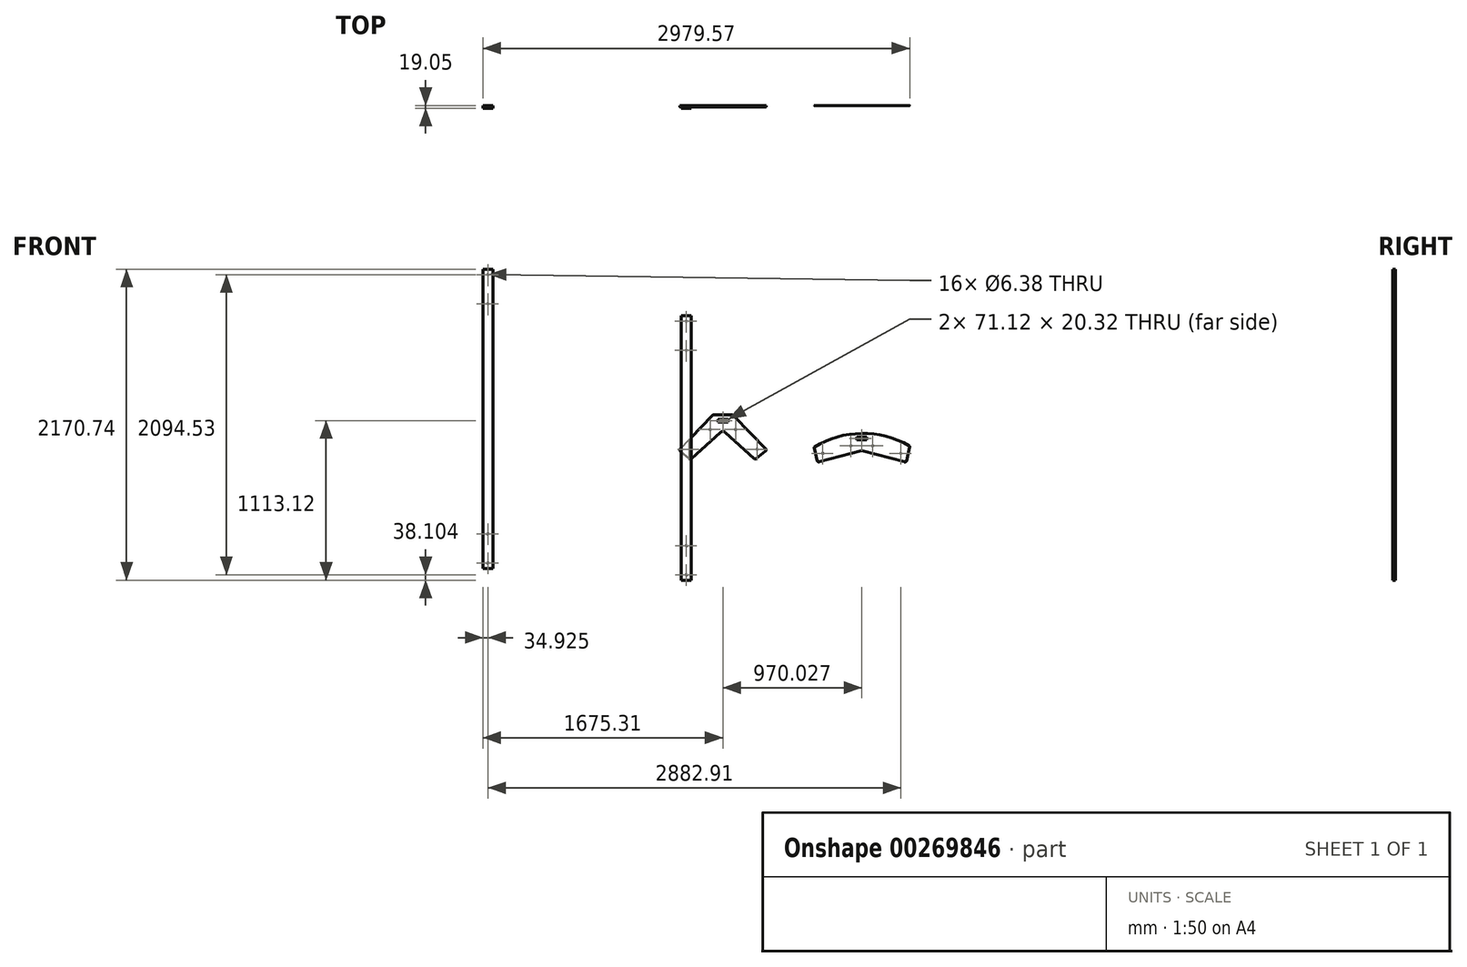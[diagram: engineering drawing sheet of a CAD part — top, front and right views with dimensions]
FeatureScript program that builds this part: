
annotation { "Feature Type Name" : "Feature", "Feature Type Description" : "" }
export const myFeature = defineFeature(function(context is Context, id is Id, definition is map)
    precondition{}
    {
        {
            var Q0;
            Q0=qCreatedBy(makeId("Front.planeOp"),FACE);
            var sketch = newSketch(context, id + "F0", { "sketchPlane" : qUnion([Q0])});
            skLineSegment(sketch, "E0.bottom", {"start": v(-21.12, -905.57) * mm, "end": v(-90.97, -905.57) * mm});
            skLineSegment(sketch, "E0.top", {"start": v(-21.12, 939.7) * mm, "end": v(-90.97, 939.7) * mm});
            skLineSegment(sketch, "E0.left", {"start": v(-21.12, -905.57) * mm, "end": v(-21.12, 939.7) * mm});
            skLineSegment(sketch, "E0.right", {"start": v(-90.97, -905.57) * mm, "end": v(-90.97, 939.7) * mm});
            skLineSegment(sketch, "E1.bottom", {"start": v(-1404.82, -823.6) * mm, "end": v(-1474.67, -823.6) * mm});
            skLineSegment(sketch, "E1.top", {"start": v(-1404.82, 1265.17) * mm, "end": v(-1474.67, 1265.17) * mm});
            skLineSegment(sketch, "E1.left", {"start": v(-1404.82, -823.6) * mm, "end": v(-1404.82, 1265.17) * mm});
            skLineSegment(sketch, "E1.right", {"start": v(-1474.67, -823.6) * mm, "end": v(-1474.67, 1265.17) * mm});
            skLineSegment(sketch, "E2", {"start": v(1170.66, 233.89) * mm, "end": v(1170.66, 0) * mm, "construction": true});
            skLineSegment(sketch, "E3", {"start": v(838.18, 14.85) * mm, "end": v(857.28, -70.28) * mm});
            skLineSegment(sketch, "E4", {"start": v(872.96, -79.77) * mm, "end": v(1167.38, -0.88) * mm});
            skLineSegment(sketch, "E5.MirrorCS", {"start": v(1504.59, 21.27) * mm, "end": v(1484.04, -70.28) * mm});
            skLineSegment(sketch, "E6.MirrorCS", {"start": v(1468.36, -79.77) * mm, "end": v(1173.95, -0.88) * mm});
            skLineSegment(sketch, "E7.bottom", {"start": v(1135.1, 73.36) * mm, "end": v(1206.22, 73.36) * mm});
            skLineSegment(sketch, "E7.top", {"start": v(1135.1, 93.68) * mm, "end": v(1206.22, 93.68) * mm});
            skLineSegment(sketch, "E7.left", {"start": v(1135.1, 73.36) * mm, "end": v(1135.1, 93.68) * mm});
            skLineSegment(sketch, "E7.right", {"start": v(1206.22, 73.36) * mm, "end": v(1206.22, 93.68) * mm});
            skPoint(sketch, "E7.middle", {"position": v(1170.66, 83.52) * mm});
            skPoint(sketch, "E8.visualSharp", {"position": v(1170.66, 0) * mm});
            skArc(sketch, "E8.filletArc", {"start": v(1173.95, -0.88) * mm, "mid": v(1170.66, -0.45) * mm, "end": v(1167.38, -0.88) * mm});
            skPoint(sketch, "E9.visualSharp", {"position": v(1481.15, -83.2) * mm});
            skArc(sketch, "E9.filletArc", {"start": v(1468.36, -79.77) * mm, "mid": v(1478.23, -78.37) * mm, "end": v(1484.04, -70.28) * mm});
            skPoint(sketch, "E10.visualSharp", {"position": v(860.18, -83.2) * mm});
            skArc(sketch, "E10.filletArc", {"start": v(857.28, -70.28) * mm, "mid": v(863.1, -78.37) * mm, "end": v(872.96, -79.77) * mm});
            skPoint(sketch, "E11.visualSharp", {"position": v(837.93, 15.94) * mm});
            skArc(sketch, "E11.filletArc", {"start": v(839.67, 24.15) * mm, "mid": v(838.03, 19.64) * mm, "end": v(838.18, 14.85) * mm});
            skPoint(sketch, "E12.visualSharp", {"position": v(1503.4, 15.94) * mm});
            skArc(sketch, "E12.filletArc", {"start": v(1504.59, 21.27) * mm, "mid": v(1504.22, 28.15) * mm, "end": v(1500.3, 33.82) * mm});
            skArc(sketch, "E13", {"start": v(1500.3, 33.82) * mm, "mid": v(1168.67, 119) * mm, "end": v(839.67, 24.15) * mm});
            skPoint(sketch, "E14", {"position": v(898.16, -20.43) * mm});
            skPoint(sketch, "E15", {"position": v(1094.44, 32.17) * mm});
            skCircle(sketch, "E16", {"center": v(898.16, -20.43) * mm, "radius": 3.19 * mm});
            skCircle(sketch, "E17", {"center": v(1094.44, 32.17) * mm, "radius": 3.19 * mm});
            skCircle(sketch, "E18.MirrorC", {"center": v(1246.9, 32.17) * mm, "radius": 3.19 * mm});
            skPoint(sketch, "E19.MirrorP", {"position": v(1443.17, -20.43) * mm});
            skCircle(sketch, "E20.MirrorC", {"center": v(1443.17, -20.43) * mm, "radius": 3.19 * mm});
            skCircle(sketch, "E21", {"center": v(-1439.74, 1227.07) * mm, "radius": 3.19 * mm});
            skCircle(sketch, "E22", {"center": v(-1439.74, 1023.87) * mm, "radius": 3.19 * mm});
            skCircle(sketch, "E23", {"center": v(-1439.74, -582.3) * mm, "radius": 3.19 * mm});
            skCircle(sketch, "E24", {"center": v(-1439.74, -785.5) * mm, "radius": 3.19 * mm});
            skCircle(sketch, "E25", {"center": v(-56.04, 901.6) * mm, "radius": 3.19 * mm});
            skCircle(sketch, "E26", {"center": v(-56.04, 698.4) * mm, "radius": 3.19 * mm});
            skCircle(sketch, "E27", {"center": v(-55.4, -664.27) * mm, "radius": 3.19 * mm});
            skCircle(sketch, "E28", {"center": v(-55.4, -867.47) * mm, "radius": 3.19 * mm});
            skSolve(sketch);
        }
        {
            var Q0;
            Q0=makeQuery(id+"F0.imprint","IMPRINT",FACE,{"disambiguationData":[TD([[makeQuery(id+"F0.imprint","IMPRINT",EDGE,{"derivedFrom":sQuery(id+"F0.wireOp",EDGE,"E3")}),1.0]])]});
            extrude(context, id + "F1", {"entities" : qUnion([Q0]), "depth" : 3 / 203.2 * mm});
        }
        {
            var Q0;
            Q0=qCreatedBy(makeId("Front.planeOp"),FACE);
            var sketch = newSketch(context, id + "F2", { "sketchPlane" : qUnion([Q0])});
            skLineSegment(sketch, "E29.bottom", {"start": v(-2314.97, -814.36) * mm, "end": v(-2384.82, -814.36) * mm});
            skLineSegment(sketch, "E29.top", {"start": v(-2314.97, 1274.41) * mm, "end": v(-2384.82, 1274.41) * mm});
            skLineSegment(sketch, "E29.left", {"start": v(-2314.97, -814.36) * mm, "end": v(-2314.97, 1274.41) * mm});
            skLineSegment(sketch, "E29.right", {"start": v(-2384.82, -814.36) * mm, "end": v(-2384.82, 1274.41) * mm});
            skLineSegment(sketch, "E30", {"start": v(200.64, 320.87) * mm, "end": v(200.64, 91.06) * mm, "construction": true});
            skLineSegment(sketch, "E31", {"start": v(-96.8, -4.89) * mm, "end": v(-32.6, -57.3) * mm});
            skLineSegment(sketch, "E32", {"start": v(-15.98, -56.83) * mm, "end": v(183.48, 125.94) * mm});
            skLineSegment(sketch, "E33.MirrorCS", {"start": v(417.26, -56.83) * mm, "end": v(217.8, 125.94) * mm});
            skLineSegment(sketch, "E34.MirrorCS", {"start": v(498.07, -4.89) * mm, "end": v(433.87, -57.3) * mm});
            skPoint(sketch, "E35.visualSharp", {"position": v(200.64, 141.66) * mm});
            skArc(sketch, "E35.filletArc", {"start": v(217.8, 125.94) * mm, "mid": v(200.64, 132.61) * mm, "end": v(183.48, 125.94) * mm});
            skPoint(sketch, "E36.visualSharp", {"position": v(-102.78, 0) * mm});
            skArc(sketch, "E36.filletArc", {"start": v(-101.16, 7.72) * mm, "mid": v(-100.77, 0.8) * mm, "end": v(-96.8, -4.89) * mm});
            skPoint(sketch, "E37.visualSharp", {"position": v(-24.09, -64.26) * mm});
            skArc(sketch, "E37.filletArc", {"start": v(-32.6, -57.3) * mm, "mid": v(-24.2, -60.17) * mm, "end": v(-15.98, -56.83) * mm});
            skPoint(sketch, "E38.visualSharp", {"position": v(425.36, -64.26) * mm});
            skArc(sketch, "E38.filletArc", {"start": v(417.26, -56.83) * mm, "mid": v(425.48, -60.17) * mm, "end": v(433.87, -57.3) * mm});
            skPoint(sketch, "E39.visualSharp", {"position": v(504.06, 0) * mm});
            skArc(sketch, "E39.filletArc", {"start": v(498.07, -4.89) * mm, "mid": v(502.04, 0.8) * mm, "end": v(502.43, 7.72) * mm});
            skPoint(sketch, "E40", {"position": v(-38.08, 9.05) * mm});
            skPoint(sketch, "E41", {"position": v(111.74, 146.33) * mm});
            skPoint(sketch, "E42.MirrorP", {"position": v(289.54, 146.33) * mm});
            skPoint(sketch, "E43.MirrorP", {"position": v(439.35, 9.05) * mm});
            skLineSegment(sketch, "E44.bottom", {"start": v(165.08, 197.39) * mm, "end": v(236.2, 197.39) * mm});
            skLineSegment(sketch, "E44.top", {"start": v(165.08, 217.7) * mm, "end": v(236.2, 217.7) * mm});
            skLineSegment(sketch, "E44.left", {"start": v(165.08, 197.39) * mm, "end": v(165.08, 217.7) * mm});
            skLineSegment(sketch, "E44.right", {"start": v(236.2, 197.39) * mm, "end": v(236.2, 217.7) * mm});
            skPoint(sketch, "E44.middle", {"position": v(200.64, 207.55) * mm});
            skLineSegment(sketch, "E45", {"start": v(-101.16, 7.72) * mm, "end": v(122.3, 240.67) * mm});
            skLineSegment(sketch, "E46", {"start": v(140.63, 248.49) * mm, "end": v(200.64, 248.49) * mm});
            skPoint(sketch, "E47.visualSharp", {"position": v(129.8, 248.49) * mm});
            skArc(sketch, "E47.filletArc", {"start": v(140.63, 248.49) * mm, "mid": v(130.67, 246.45) * mm, "end": v(122.3, 240.67) * mm});
            skLineSegment(sketch, "E48.MirrorCS", {"start": v(260.64, 248.49) * mm, "end": v(200.64, 248.49) * mm});
            skLineSegment(sketch, "E49.MirrorCS", {"start": v(502.43, 7.72) * mm, "end": v(278.97, 240.67) * mm});
            skArc(sketch, "E50.MirrorCS", {"start": v(260.64, 248.49) * mm, "mid": v(270.6, 246.45) * mm, "end": v(278.97, 240.67) * mm});
            skPoint(sketch, "E51.MirrorP", {"position": v(271.48, 248.49) * mm});
            skCircle(sketch, "E52", {"center": v(111.74, 146.33) * mm, "radius": 3.19 * mm});
            skCircle(sketch, "E53", {"center": v(-38.08, 9.05) * mm, "radius": 3.19 * mm});
            skCircle(sketch, "E54", {"center": v(289.54, 146.33) * mm, "radius": 3.19 * mm});
            skCircle(sketch, "E55", {"center": v(439.35, 9.05) * mm, "radius": 3.19 * mm});
            skSolve(sketch);
        }
        {
            var Q0;
            Q0=makeQuery(id+"F2.imprint","IMPRINT",FACE,{"disambiguationData":[TD([[makeQuery(id+"F2.imprint","IMPRINT",EDGE,{"derivedFrom":sQuery(id+"F2.wireOp",EDGE,"E31")}),1.0]])]});
            extrude(context, id + "F3", {"entities" : qUnion([Q0]), "depth" : 9.52 * mm});
        }
        {
            var Q0;
            Q0=makeQuery(id+"F0.imprint","IMPRINT",FACE,{"disambiguationData":[TD([[makeQuery(id+"F0.imprint","IMPRINT",EDGE,{"derivedFrom":sQuery(id+"F0.wireOp",EDGE,"E1.bottom")}),-1.0]])]});
            var Q1;
            Q1=makeQuery(id+"F0.imprint","IMPRINT",FACE,{"disambiguationData":[TD([[makeQuery(id+"F0.imprint","IMPRINT",EDGE,{"derivedFrom":sQuery(id+"F0.wireOp",EDGE,"E0.bottom")}),-1.0]])]});
            extrude(context, id + "F4", {"entities" : qUnion([Q0, Q1]), "depth" : 19.05 * mm});
        }
    });
